# Revit family: ASL_64_Series_glazing_mullion_wide
name_source: partatom
category: Detail Items
revit_build: Autodesk Revit 2018 (Build: 20170223_1515(x64)
units: mm (PartAtom-declared; Revit-internal decimal feet)

## family parameters
Rotate with component = No
Section Shape = Not Defined
Shared = Yes

## types (3) — shared parameters
Flush Infill_1 = No
Flush Infill_2 = No
Glazing Extension_1 = Yes
Glazing Extension_2 = Yes
Glazing Side_1 = Yes
Glazing Side_2 = Yes
Manufacturer = Aluminate Solutions Limited
Technical Info = www.aluminate.nz
Type Comments = ASL 64 Series Wide Mullion With Glazing

## per-type parameters (varying)
| type | Flush Infill_4 | Flush Starter Cap | Glazing Extension_3 | Glazing Extension_4 | Glazing Side_3 | Glazing Side_4 |
| 4 Side Glazing | No | No | Yes | Yes | Yes | Yes |
| 3 Side Glazing | Yes | No | Yes | No | Yes | No |
| 2 Side Glazing | Yes | Yes | No | No | No | No |

## geometry (parser evidence)
native form markers: Sweep x5
no freeform markers — native parametric forms only
